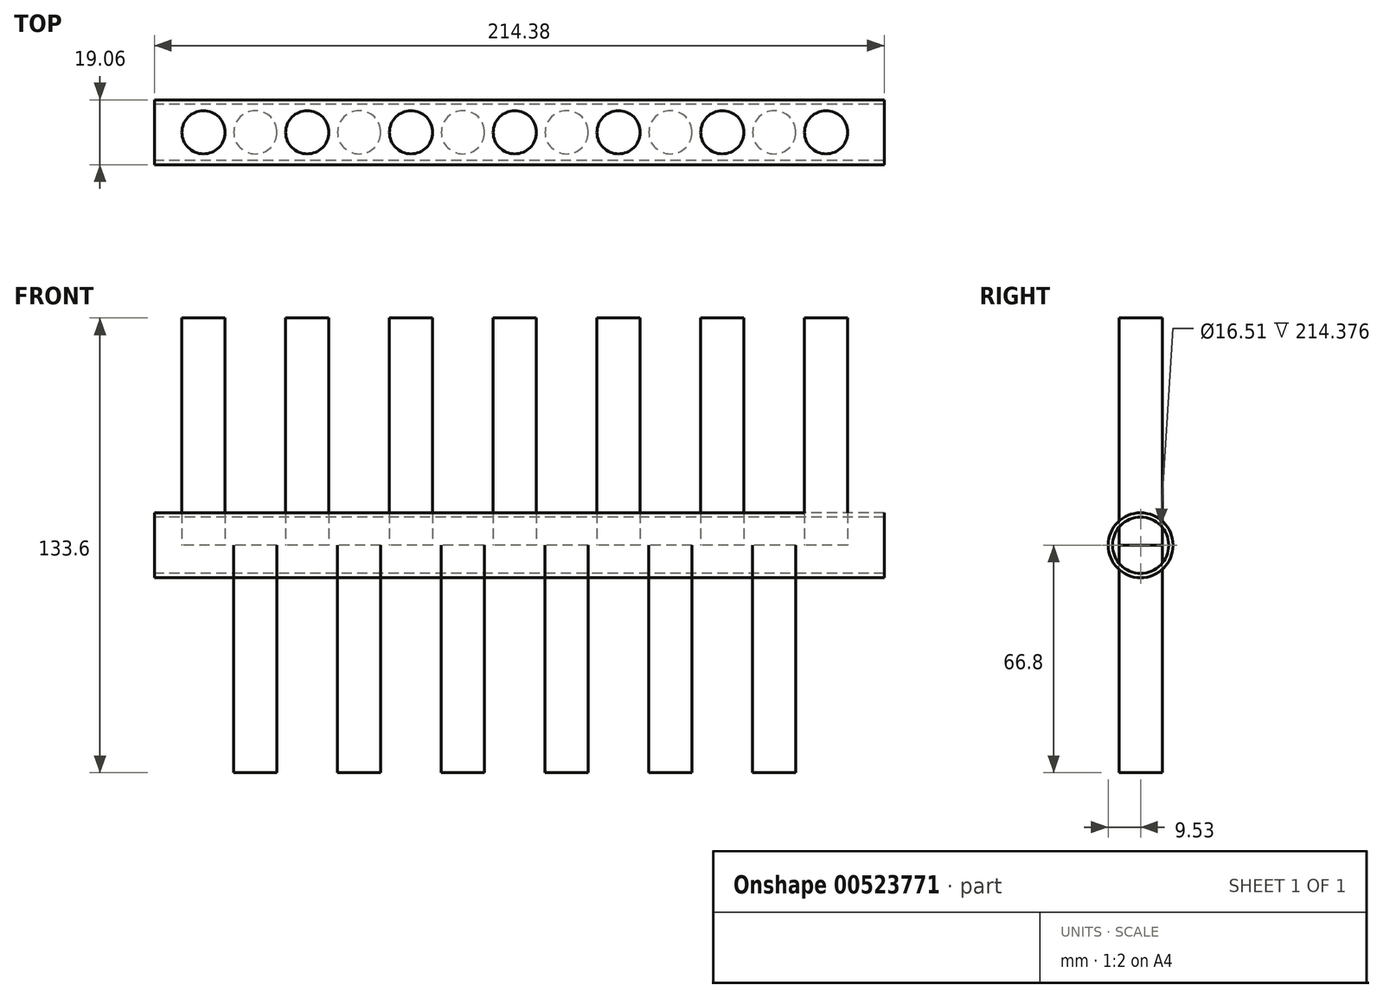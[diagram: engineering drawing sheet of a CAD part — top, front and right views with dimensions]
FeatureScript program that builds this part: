
annotation { "Feature Type Name" : "Feature", "Feature Type Description" : "" }
export const myFeature = defineFeature(function(context is Context, id is Id, definition is map)
    precondition{}
    {
        {
            var Q0;
            Q0=qCreatedBy(makeId("Right.planeOp"),FACE);
            var sketch = newSketch(context, id + "F0", { "sketchPlane" : qUnion([Q0])});
            skCircle(sketch, "E0", {"center": v(0, 0) * mm, "radius": 9.53 * mm});
            skCircle(sketch, "E1", {"center": v(0, 0) * mm, "radius": 8.26 * mm});
            skSolve(sketch);
        }
        {
            var Q0;
            Q0=makeQuery(id+"F0.imprint","IMPRINT",FACE,{"disambiguationData":[TD([[makeQuery(id+"F0.imprint","IMPRINT",EDGE,{"derivedFrom":sQuery(id+"F0.wireOp",EDGE,"E0")}),1.0]])]});
            extrude(context, id + "F1", {"entities" : qUnion([Q0]), "depth" : 214.38 * mm, "offsetDistance" : 25.4 * mm});
        }
        {
            var Q0;
            Q0=qCreatedBy(makeId("Top.planeOp"),FACE);
            var sketch = newSketch(context, id + "F2", { "sketchPlane" : qUnion([Q0])});
            skLineSegment(sketch, "E2", {"start": v(0, 0) * mm, "end": v(214.37, 0) * mm});
            skLineSegment(sketch, "E3", {"start": v(0, 0) * mm, "end": v(8.07, 0) * mm});
            skLineSegment(sketch, "E4", {"start": v(8.07, 0) * mm, "end": v(14.42, 0) * mm});
            skCircle(sketch, "E5", {"center": v(14.42, 0) * mm, "radius": 6.35 * mm});
            skCircle(sketch, "E6.1.0.0", {"center": v(29.66, 0) * mm, "radius": 6.35 * mm});
            skCircle(sketch, "E6.2.0.0", {"center": v(44.9, 0) * mm, "radius": 6.35 * mm});
            skCircle(sketch, "E6.3.0.0", {"center": v(60.14, 0) * mm, "radius": 6.35 * mm});
            skCircle(sketch, "E6.4.0.0", {"center": v(75.38, 0) * mm, "radius": 6.35 * mm});
            skCircle(sketch, "E6.5.0.0", {"center": v(90.62, 0) * mm, "radius": 6.35 * mm});
            skCircle(sketch, "E6.6.0.0", {"center": v(105.86, 0) * mm, "radius": 6.35 * mm});
            skCircle(sketch, "E6.7.0.0", {"center": v(121.1, 0) * mm, "radius": 6.35 * mm});
            skCircle(sketch, "E6.8.0.0", {"center": v(136.34, 0) * mm, "radius": 6.35 * mm});
            skCircle(sketch, "E6.9.0.0", {"center": v(151.58, 0) * mm, "radius": 6.35 * mm});
            skCircle(sketch, "E6.10.0.0", {"center": v(166.82, 0) * mm, "radius": 6.35 * mm});
            skCircle(sketch, "E6.11.0.0", {"center": v(182.06, 0) * mm, "radius": 6.35 * mm});
            skCircle(sketch, "E6.12.0.0", {"center": v(197.3, 0) * mm, "radius": 6.35 * mm});
            skLineSegment(sketch, "E6.direction1", {"start": v(14.42, 0) * mm, "end": v(29.66, 0) * mm, "construction": true});
            skLineSegment(sketch, "E7", {"start": v(198.6, 0) * mm, "end": v(214.37, 0) * mm});
            skSolve(sketch);
        }
        {
            var Q0;
            {var subQ0=sQuery(id+"F2.wireOp",EDGE,"E2");var subQ1=makeQuery(id+"F2.imprint","IMPRINT",VERTEX,{"disambiguationData":[OD(1.0)],"derivedFrom":subQ0});Q0=makeQuery(id+"F2.imprint","IMPRINT",FACE,{"disambiguationData":[TD([[makeQuery(id+"F2.imprint","IMPRINT",EDGE,{"disambiguationData":[TD([[subQ1,-1.0]])],"derivedFrom":subQ0}),-1.0]])]});}
            var Q1;
            {var subQ0=sQuery(id+"F2.wireOp",EDGE,"E6.2.0.0");var subQ1=sQuery(id+"F2.wireOp",EDGE,"E2");var subQ2=makeQuery(id+"F2.imprint","INTERSECT",VERTEX,{"disambiguationData":[OD(0.0)],"derivedFrom":[subQ1,subQ0]});Q1=makeQuery(id+"F2.imprint","IMPRINT",FACE,{"disambiguationData":[TD([[makeQuery(id+"F2.imprint","IMPRINT",EDGE,{"disambiguationData":[TD([[subQ2,-1.0]])],"derivedFrom":subQ1}),1.0]])]});}
            var Q2;
            {var subQ0=sQuery(id+"F2.wireOp",EDGE,"E6.2.0.0");var subQ1=sQuery(id+"F2.wireOp",EDGE,"E2");var subQ2=makeQuery(id+"F2.imprint","INTERSECT",VERTEX,{"disambiguationData":[OD(0.0)],"derivedFrom":[subQ1,subQ0]});Q2=makeQuery(id+"F2.imprint","IMPRINT",FACE,{"disambiguationData":[TD([[makeQuery(id+"F2.imprint","IMPRINT",EDGE,{"disambiguationData":[TD([[subQ2,-1.0]])],"derivedFrom":subQ1}),-1.0]])]});}
            var Q3;
            {var subQ0=sQuery(id+"F2.wireOp",EDGE,"E2");var subQ1=makeQuery(id+"F2.imprint","IMPRINT",VERTEX,{"disambiguationData":[OD(1.0)],"derivedFrom":subQ0});Q3=makeQuery(id+"F2.imprint","IMPRINT",FACE,{"disambiguationData":[TD([[makeQuery(id+"F2.imprint","IMPRINT",EDGE,{"disambiguationData":[TD([[subQ1,-1.0]])],"derivedFrom":subQ0}),1.0]])]});}
            var Q4;
            {var subQ0=sQuery(id+"F2.wireOp",EDGE,"E6.4.0.0");var subQ1=sQuery(id+"F2.wireOp",EDGE,"E2");var subQ2=makeQuery(id+"F2.imprint","INTERSECT",VERTEX,{"disambiguationData":[OD(0.0)],"derivedFrom":[subQ1,subQ0]});Q4=makeQuery(id+"F2.imprint","IMPRINT",FACE,{"disambiguationData":[TD([[makeQuery(id+"F2.imprint","IMPRINT",EDGE,{"disambiguationData":[TD([[subQ2,-1.0]])],"derivedFrom":subQ1}),1.0]])]});}
            var Q5;
            {var subQ0=sQuery(id+"F2.wireOp",EDGE,"E6.4.0.0");var subQ1=sQuery(id+"F2.wireOp",EDGE,"E2");var subQ2=makeQuery(id+"F2.imprint","INTERSECT",VERTEX,{"disambiguationData":[OD(0.0)],"derivedFrom":[subQ1,subQ0]});Q5=makeQuery(id+"F2.imprint","IMPRINT",FACE,{"disambiguationData":[TD([[makeQuery(id+"F2.imprint","IMPRINT",EDGE,{"disambiguationData":[TD([[subQ2,-1.0]])],"derivedFrom":subQ1}),-1.0]])]});}
            var Q6;
            {var subQ0=sQuery(id+"F2.wireOp",EDGE,"E6.6.0.0");var subQ1=sQuery(id+"F2.wireOp",EDGE,"E2");var subQ2=makeQuery(id+"F2.imprint","INTERSECT",VERTEX,{"disambiguationData":[OD(0.0)],"derivedFrom":[subQ1,subQ0]});Q6=makeQuery(id+"F2.imprint","IMPRINT",FACE,{"disambiguationData":[TD([[makeQuery(id+"F2.imprint","IMPRINT",EDGE,{"disambiguationData":[TD([[subQ2,-1.0]])],"derivedFrom":subQ1}),1.0]])]});}
            var Q7;
            {var subQ0=sQuery(id+"F2.wireOp",EDGE,"E6.6.0.0");var subQ1=sQuery(id+"F2.wireOp",EDGE,"E2");var subQ2=makeQuery(id+"F2.imprint","INTERSECT",VERTEX,{"disambiguationData":[OD(0.0)],"derivedFrom":[subQ1,subQ0]});Q7=makeQuery(id+"F2.imprint","IMPRINT",FACE,{"disambiguationData":[TD([[makeQuery(id+"F2.imprint","IMPRINT",EDGE,{"disambiguationData":[TD([[subQ2,-1.0]])],"derivedFrom":subQ1}),-1.0]])]});}
            var Q8;
            {var subQ0=sQuery(id+"F2.wireOp",EDGE,"E6.8.0.0");var subQ1=sQuery(id+"F2.wireOp",EDGE,"E2");var subQ2=makeQuery(id+"F2.imprint","INTERSECT",VERTEX,{"disambiguationData":[OD(0.0)],"derivedFrom":[subQ1,subQ0]});Q8=makeQuery(id+"F2.imprint","IMPRINT",FACE,{"disambiguationData":[TD([[makeQuery(id+"F2.imprint","IMPRINT",EDGE,{"disambiguationData":[TD([[subQ2,-1.0]])],"derivedFrom":subQ1}),1.0]])]});}
            var Q9;
            {var subQ0=sQuery(id+"F2.wireOp",EDGE,"E6.8.0.0");var subQ1=sQuery(id+"F2.wireOp",EDGE,"E2");var subQ2=makeQuery(id+"F2.imprint","INTERSECT",VERTEX,{"disambiguationData":[OD(0.0)],"derivedFrom":[subQ1,subQ0]});Q9=makeQuery(id+"F2.imprint","IMPRINT",FACE,{"disambiguationData":[TD([[makeQuery(id+"F2.imprint","IMPRINT",EDGE,{"disambiguationData":[TD([[subQ2,-1.0]])],"derivedFrom":subQ1}),-1.0]])]});}
            var Q10;
            {var subQ0=sQuery(id+"F2.wireOp",EDGE,"E6.10.0.0");var subQ1=sQuery(id+"F2.wireOp",EDGE,"E2");var subQ2=makeQuery(id+"F2.imprint","INTERSECT",VERTEX,{"disambiguationData":[OD(0.0)],"derivedFrom":[subQ1,subQ0]});Q10=makeQuery(id+"F2.imprint","IMPRINT",FACE,{"disambiguationData":[TD([[makeQuery(id+"F2.imprint","IMPRINT",EDGE,{"disambiguationData":[TD([[subQ2,-1.0]])],"derivedFrom":subQ1}),1.0]])]});}
            var Q11;
            {var subQ0=sQuery(id+"F2.wireOp",EDGE,"E6.10.0.0");var subQ1=sQuery(id+"F2.wireOp",EDGE,"E2");var subQ2=makeQuery(id+"F2.imprint","INTERSECT",VERTEX,{"disambiguationData":[OD(0.0)],"derivedFrom":[subQ1,subQ0]});Q11=makeQuery(id+"F2.imprint","IMPRINT",FACE,{"disambiguationData":[TD([[makeQuery(id+"F2.imprint","IMPRINT",EDGE,{"disambiguationData":[TD([[subQ2,-1.0]])],"derivedFrom":subQ1}),-1.0]])]});}
            var Q12;
            {var subQ0=sQuery(id+"F2.wireOp",EDGE,"E2");var subQ1=makeQuery(id+"F2.imprint","IMPRINT",VERTEX,{"disambiguationData":[OD(0.0)],"derivedFrom":subQ0});Q12=makeQuery(id+"F2.imprint","IMPRINT",FACE,{"disambiguationData":[TD([[makeQuery(id+"F2.imprint","IMPRINT",EDGE,{"disambiguationData":[TD([[subQ1,1.0]])],"derivedFrom":subQ0}),1.0]])]});}
            var Q13;
            {var subQ0=sQuery(id+"F2.wireOp",EDGE,"E2");var subQ1=makeQuery(id+"F2.imprint","IMPRINT",VERTEX,{"disambiguationData":[OD(0.0)],"derivedFrom":subQ0});Q13=makeQuery(id+"F2.imprint","IMPRINT",FACE,{"disambiguationData":[TD([[makeQuery(id+"F2.imprint","IMPRINT",EDGE,{"disambiguationData":[TD([[subQ1,1.0]])],"derivedFrom":subQ0}),-1.0]])]});}
            extrude(context, id + "F3", {"entities" : qUnion([Q0, Q1, Q2, Q3, Q4, Q5, Q6, Q7, Q8, Q9, Q10, Q11, Q12, Q13]), "depth" : 66.8 * mm, "offsetDistance" : 25.4 * mm});
        }
        {
            var Q0;
            {var subQ0=sQuery(id+"F2.wireOp",EDGE,"E6.1.0.0");var subQ1=sQuery(id+"F2.wireOp",EDGE,"E2");var subQ2=makeQuery(id+"F2.imprint","INTERSECT",VERTEX,{"disambiguationData":[OD(0.0)],"derivedFrom":[subQ1,subQ0]});Q0=makeQuery(id+"F2.imprint","IMPRINT",FACE,{"disambiguationData":[TD([[makeQuery(id+"F2.imprint","IMPRINT",EDGE,{"disambiguationData":[TD([[subQ2,-1.0]])],"derivedFrom":subQ1}),-1.0]])]});}
            var Q1;
            {var subQ0=sQuery(id+"F2.wireOp",EDGE,"E6.1.0.0");var subQ1=sQuery(id+"F2.wireOp",EDGE,"E2");var subQ2=makeQuery(id+"F2.imprint","INTERSECT",VERTEX,{"disambiguationData":[OD(0.0)],"derivedFrom":[subQ1,subQ0]});Q1=makeQuery(id+"F2.imprint","IMPRINT",FACE,{"disambiguationData":[TD([[makeQuery(id+"F2.imprint","IMPRINT",EDGE,{"disambiguationData":[TD([[subQ2,-1.0]])],"derivedFrom":subQ1}),1.0]])]});}
            var Q2;
            {var subQ0=sQuery(id+"F2.wireOp",EDGE,"E6.3.0.0");var subQ1=sQuery(id+"F2.wireOp",EDGE,"E2");var subQ2=makeQuery(id+"F2.imprint","INTERSECT",VERTEX,{"disambiguationData":[OD(0.0)],"derivedFrom":[subQ1,subQ0]});Q2=makeQuery(id+"F2.imprint","IMPRINT",FACE,{"disambiguationData":[TD([[makeQuery(id+"F2.imprint","IMPRINT",EDGE,{"disambiguationData":[TD([[subQ2,-1.0]])],"derivedFrom":subQ1}),1.0]])]});}
            var Q3;
            {var subQ0=sQuery(id+"F2.wireOp",EDGE,"E6.3.0.0");var subQ1=sQuery(id+"F2.wireOp",EDGE,"E2");var subQ2=makeQuery(id+"F2.imprint","INTERSECT",VERTEX,{"disambiguationData":[OD(0.0)],"derivedFrom":[subQ1,subQ0]});Q3=makeQuery(id+"F2.imprint","IMPRINT",FACE,{"disambiguationData":[TD([[makeQuery(id+"F2.imprint","IMPRINT",EDGE,{"disambiguationData":[TD([[subQ2,-1.0]])],"derivedFrom":subQ1}),-1.0]])]});}
            var Q4;
            {var subQ0=sQuery(id+"F2.wireOp",EDGE,"E6.5.0.0");var subQ1=sQuery(id+"F2.wireOp",EDGE,"E2");var subQ2=makeQuery(id+"F2.imprint","INTERSECT",VERTEX,{"disambiguationData":[OD(0.0)],"derivedFrom":[subQ1,subQ0]});Q4=makeQuery(id+"F2.imprint","IMPRINT",FACE,{"disambiguationData":[TD([[makeQuery(id+"F2.imprint","IMPRINT",EDGE,{"disambiguationData":[TD([[subQ2,-1.0]])],"derivedFrom":subQ1}),1.0]])]});}
            var Q5;
            {var subQ0=sQuery(id+"F2.wireOp",EDGE,"E6.5.0.0");var subQ1=sQuery(id+"F2.wireOp",EDGE,"E2");var subQ2=makeQuery(id+"F2.imprint","INTERSECT",VERTEX,{"disambiguationData":[OD(0.0)],"derivedFrom":[subQ1,subQ0]});Q5=makeQuery(id+"F2.imprint","IMPRINT",FACE,{"disambiguationData":[TD([[makeQuery(id+"F2.imprint","IMPRINT",EDGE,{"disambiguationData":[TD([[subQ2,-1.0]])],"derivedFrom":subQ1}),-1.0]])]});}
            var Q6;
            {var subQ0=sQuery(id+"F2.wireOp",EDGE,"E6.7.0.0");var subQ1=sQuery(id+"F2.wireOp",EDGE,"E2");var subQ2=makeQuery(id+"F2.imprint","INTERSECT",VERTEX,{"disambiguationData":[OD(0.0)],"derivedFrom":[subQ1,subQ0]});Q6=makeQuery(id+"F2.imprint","IMPRINT",FACE,{"disambiguationData":[TD([[makeQuery(id+"F2.imprint","IMPRINT",EDGE,{"disambiguationData":[TD([[subQ2,-1.0]])],"derivedFrom":subQ1}),1.0]])]});}
            var Q7;
            {var subQ0=sQuery(id+"F2.wireOp",EDGE,"E6.7.0.0");var subQ1=sQuery(id+"F2.wireOp",EDGE,"E2");var subQ2=makeQuery(id+"F2.imprint","INTERSECT",VERTEX,{"disambiguationData":[OD(0.0)],"derivedFrom":[subQ1,subQ0]});Q7=makeQuery(id+"F2.imprint","IMPRINT",FACE,{"disambiguationData":[TD([[makeQuery(id+"F2.imprint","IMPRINT",EDGE,{"disambiguationData":[TD([[subQ2,-1.0]])],"derivedFrom":subQ1}),-1.0]])]});}
            var Q8;
            {var subQ0=sQuery(id+"F2.wireOp",EDGE,"E6.9.0.0");var subQ1=sQuery(id+"F2.wireOp",EDGE,"E2");var subQ2=makeQuery(id+"F2.imprint","INTERSECT",VERTEX,{"disambiguationData":[OD(0.0)],"derivedFrom":[subQ1,subQ0]});Q8=makeQuery(id+"F2.imprint","IMPRINT",FACE,{"disambiguationData":[TD([[makeQuery(id+"F2.imprint","IMPRINT",EDGE,{"disambiguationData":[TD([[subQ2,-1.0]])],"derivedFrom":subQ1}),1.0]])]});}
            var Q9;
            {var subQ0=sQuery(id+"F2.wireOp",EDGE,"E6.9.0.0");var subQ1=sQuery(id+"F2.wireOp",EDGE,"E2");var subQ2=makeQuery(id+"F2.imprint","INTERSECT",VERTEX,{"disambiguationData":[OD(0.0)],"derivedFrom":[subQ1,subQ0]});Q9=makeQuery(id+"F2.imprint","IMPRINT",FACE,{"disambiguationData":[TD([[makeQuery(id+"F2.imprint","IMPRINT",EDGE,{"disambiguationData":[TD([[subQ2,-1.0]])],"derivedFrom":subQ1}),-1.0]])]});}
            var Q10;
            {var subQ0=sQuery(id+"F2.wireOp",EDGE,"E6.11.0.0");var subQ1=sQuery(id+"F2.wireOp",EDGE,"E2");var subQ2=makeQuery(id+"F2.imprint","INTERSECT",VERTEX,{"disambiguationData":[OD(0.0)],"derivedFrom":[subQ1,subQ0]});Q10=makeQuery(id+"F2.imprint","IMPRINT",FACE,{"disambiguationData":[TD([[makeQuery(id+"F2.imprint","IMPRINT",EDGE,{"disambiguationData":[TD([[subQ2,-1.0]])],"derivedFrom":subQ1}),1.0]])]});}
            var Q11;
            {var subQ0=sQuery(id+"F2.wireOp",EDGE,"E6.11.0.0");var subQ1=sQuery(id+"F2.wireOp",EDGE,"E2");var subQ2=makeQuery(id+"F2.imprint","INTERSECT",VERTEX,{"disambiguationData":[OD(0.0)],"derivedFrom":[subQ1,subQ0]});Q11=makeQuery(id+"F2.imprint","IMPRINT",FACE,{"disambiguationData":[TD([[makeQuery(id+"F2.imprint","IMPRINT",EDGE,{"disambiguationData":[TD([[subQ2,-1.0]])],"derivedFrom":subQ1}),-1.0]])]});}
            extrude(context, id + "F4", {"entities" : qUnion([Q0, Q1, Q2, Q3, Q4, Q5, Q6, Q7, Q8, Q9, Q10, Q11]), "oppositeDirection" : true, "depth" : 66.8 * mm, "offsetDistance" : 25.4 * mm});
        }
    });
